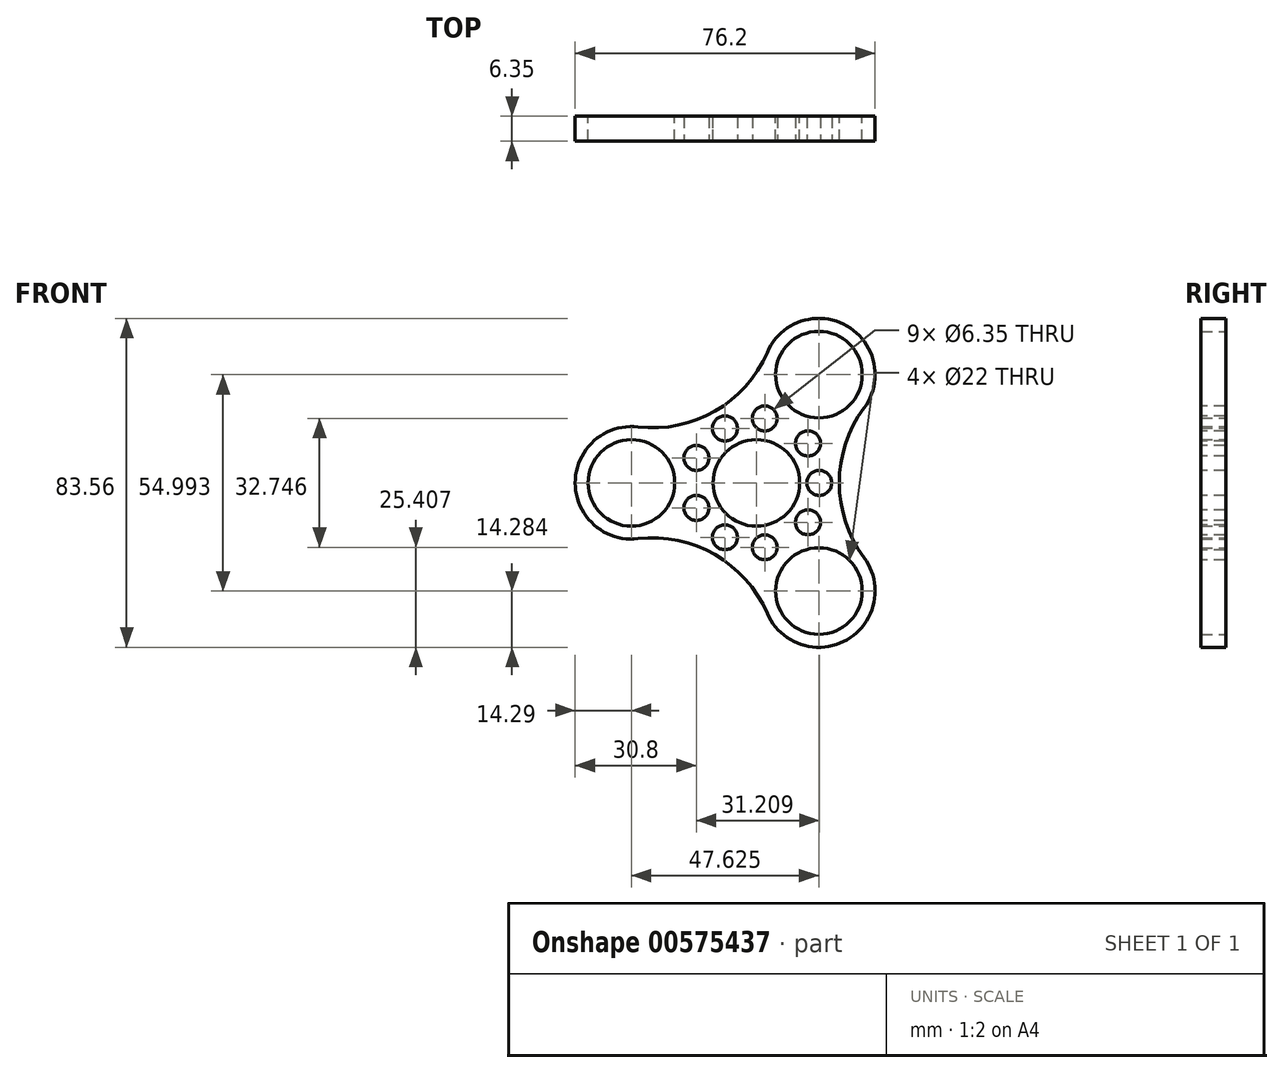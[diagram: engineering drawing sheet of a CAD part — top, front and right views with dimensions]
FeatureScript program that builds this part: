
annotation { "Feature Type Name" : "Feature", "Feature Type Description" : "" }
export const myFeature = defineFeature(function(context is Context, id is Id, definition is map)
    precondition{}
    {
        {
            var Q0;
            Q0=qCreatedBy(makeId("Front.planeOp"),FACE);
            var sketch = newSketch(context, id + "F0", { "sketchPlane" : qUnion([Q0])});
            skCircle(sketch, "E0", {"center": v(0, 0) * mm, "radius": 14.29 * mm});
            skCircle(sketch, "E1", {"center": v(0, 0) * mm, "radius": 11 * mm});
            skCircle(sketch, "E2", {"center": v(-31.75, 0) * mm, "radius": 14.29 * mm});
            skCircle(sketch, "E3", {"center": v(-31.75, 0) * mm, "radius": 11 * mm});
            skCircle(sketch, "E4.1.0", {"center": v(15.87, -27.5) * mm, "radius": 14.29 * mm});
            skCircle(sketch, "E4.2.0", {"center": v(15.88, 27.5) * mm, "radius": 14.29 * mm});
            skCircle(sketch, "E5", {"center": v(15.88, 27.5) * mm, "radius": 11 * mm});
            skCircle(sketch, "E6", {"center": v(15.87, -27.5) * mm, "radius": 11 * mm});
            skSolve(sketch);
        }
        {
            var Q0;
            Q0=makeQuery(id+"FFv1Rk9DyuZzD2w_0.imprint","IMPRINT",FACE,{"disambiguationData":[TD([[makeQuery(id+"FFv1Rk9DyuZzD2w_0.imprint","IMPRINT",EDGE,{"derivedFrom":sQuery(id+"FFv1Rk9DyuZzD2w_0.wireOp",EDGE,"BiCupdTj-Y5xa-yT44-ajqj-lFmwiwwpYxpl")}),1.0]])]});
            var sketch = newSketch(context, id + "F1", { "sketchPlane" : qUnion([Q0])});
            skCircle(sketch, "E7", {"center": v(0, 46.13) * mm, "radius": 31.85 * mm});
            skCircle(sketch, "E8", {"center": v(-29.85, 35.03) * mm, "radius": 20.68 * mm});
            skCircle(sketch, "E9", {"center": v(29.93, 35.25) * mm, "radius": 20.68 * mm});
            skCircle(sketch, "E10", {"center": v(0, -46.09) * mm, "radius": 31.8 * mm});
            skCircle(sketch, "E11", {"center": v(-29.8, -35.02) * mm, "radius": 20.68 * mm});
            skCircle(sketch, "E12", {"center": v(29.8, -35.02) * mm, "radius": 20.68 * mm});
            skSolve(sketch);
        }
        {
            var Q0;
            Q0=qCreatedBy(makeId("Front.planeOp"),FACE);
            var sketch = newSketch(context, id + "F2", { "sketchPlane" : qUnion([Q0])});
            skCircle(sketch, "E13.0", {"center": v(-31.75, 0) * mm, "radius": 14.29 * mm});
            skCircle(sketch, "E14.0", {"center": v(15.88, 27.5) * mm, "radius": 14.29 * mm});
            skCircle(sketch, "E15.0", {"center": v(15.87, -27.5) * mm, "radius": 14.29 * mm});
            skCircle(sketch, "E16.0", {"center": v(0, 0) * mm, "radius": 14.29 * mm});
            skCircle(sketch, "E17.0", {"center": v(-31.75, 0) * mm, "radius": 11 * mm});
            skCircle(sketch, "E18.0", {"center": v(0, 0) * mm, "radius": 11 * mm});
            skCircle(sketch, "E19.0", {"center": v(15.87, -27.5) * mm, "radius": 11 * mm});
            skCircle(sketch, "E20.0", {"center": v(15.88, 27.5) * mm, "radius": 11 * mm});
            skArc(sketch, "E21", {"start": v(27.33, 18.96) * mm, "mid": v(21.05, 0) * mm, "end": v(27.33, -18.96) * mm});
            skArc(sketch, "E22", {"start": v(2.76, -33.15) * mm, "mid": v(-10.52, -18.23) * mm, "end": v(-30.09, -14.2) * mm});
            skArc(sketch, "E23", {"start": v(-30.09, 14.2) * mm, "mid": v(-10.52, 18.23) * mm, "end": v(2.76, 33.15) * mm});
            skSolve(sketch);
        }
        {
            var Q0;
            Q0=makeQuery(id+"F2.imprint","IMPRINT",FACE,{"disambiguationData":[TD([[makeQuery(id+"F2.imprint","IMPRINT",EDGE,{"derivedFrom":sQuery(id+"F2.wireOp",EDGE,"E20.0")}),-1.0]])]});
            var Q1;
            {var subQ6=sQuery(id+"F2.wireOp",EDGE,"E16.0");Q1=makeQuery(id+"F2.imprint","IMPRINT",FACE,{"disambiguationData":[TD([[makeQuery(id+"F2.imprint","IMPRINT",EDGE,{"derivedFrom":subQ6}),-1.0]])]});}
            var Q2;
            Q2=makeQuery(id+"F2.imprint","IMPRINT",FACE,{"disambiguationData":[TD([[makeQuery(id+"F2.imprint","IMPRINT",EDGE,{"derivedFrom":sQuery(id+"F2.wireOp",EDGE,"E16.0")}),1.0]])]});
            var Q3;
            Q3=makeQuery(id+"F2.imprint","IMPRINT",FACE,{"disambiguationData":[TD([[makeQuery(id+"F2.imprint","IMPRINT",EDGE,{"derivedFrom":sQuery(id+"F2.wireOp",EDGE,"E17.0")}),-1.0]])]});
            var Q4;
            Q4=makeQuery(id+"F2.imprint","IMPRINT",FACE,{"disambiguationData":[TD([[makeQuery(id+"F2.imprint","IMPRINT",EDGE,{"derivedFrom":sQuery(id+"F2.wireOp",EDGE,"E19.0")}),-1.0]])]});
            extrude(context, id + "F3", {"entities" : qUnion([Q0, Q1, Q2, Q3, Q4]), "depth" : 6.35 * mm, "offsetDistance" : 25.4 * mm});
        }
        {
            var Q0;
            Q0=makeQuery(id+"F3.opExtrude","CAP_FACE",FACE,{"disambiguationData":[OSD([sQuery(id+"F2.wireOp",EDGE,"E13.0"),sQuery(id+"F2.wireOp",EDGE,"E14.0"),sQuery(id+"F2.wireOp",EDGE,"E15.0"),sQuery(id+"F2.wireOp",EDGE,"E17.0"),sQuery(id+"F2.wireOp",EDGE,"E18.0"),sQuery(id+"F2.wireOp",EDGE,"E19.0"),sQuery(id+"F2.wireOp",EDGE,"E20.0"),sQuery(id+"F2.wireOp",EDGE,"E21"),sQuery(id+"F2.wireOp",EDGE,"E22"),sQuery(id+"F2.wireOp",EDGE,"E23")])],"isStart":false});
            var sketch = newSketch(context, id + "F4", { "sketchPlane" : qUnion([Q0])});
            skCircle(sketch, "E24", {"center": v(-15.24, 6.35) * mm, "radius": 3.18 * mm});
            skCircle(sketch, "E25", {"center": v(-15.24, -6.35) * mm, "radius": 3.18 * mm});
            skCircle(sketch, "E26.1.0", {"center": v(2.12, -16.37) * mm, "radius": 3.18 * mm});
            skCircle(sketch, "E26.1.1", {"center": v(13.12, -10.02) * mm, "radius": 3.18 * mm});
            skCircle(sketch, "E26.2.0", {"center": v(13.12, 10.02) * mm, "radius": 3.18 * mm});
            skCircle(sketch, "E26.2.1", {"center": v(2.12, 16.37) * mm, "radius": 3.18 * mm});
            skPoint(sketch, "E26.center", {"position": v(0, 0) * mm});
            skSolve(sketch);
        }
        {
            var Q0;
            Q0=makeQuery(id+"F4.imprint","IMPRINT",FACE,{"disambiguationData":[TD([[makeQuery(id+"F4.imprint","IMPRINT",EDGE,{"derivedFrom":sQuery(id+"F4.wireOp",EDGE,"E24")}),-1.0]])]});
            var sketch = newSketch(context, id + "F5", { "sketchPlane" : qUnion([Q0])});
            skCircle(sketch, "E27", {"center": v(15.97, 0) * mm, "radius": 3.18 * mm});
            skCircle(sketch, "E28.1.0", {"center": v(-7.98, 13.83) * mm, "radius": 3.18 * mm});
            skCircle(sketch, "E28.2.0", {"center": v(-7.98, -13.83) * mm, "radius": 3.18 * mm});
            skPoint(sketch, "E28.center", {"position": v(0, 0) * mm});
            skSolve(sketch);
        }
        {
            var Q0;
            Q0=makeQuery(id+"F4.imprint","IMPRINT",FACE,{"disambiguationData":[TD([[makeQuery(id+"F4.imprint","IMPRINT",EDGE,{"derivedFrom":sQuery(id+"F4.wireOp",EDGE,"E24")}),1.0]])]});
            var Q1;
            Q1=makeQuery(id+"F5.imprint","IMPRINT",FACE,{"disambiguationData":[TD([[makeQuery(id+"F5.imprint","IMPRINT",EDGE,{"derivedFrom":sQuery(id+"F5.wireOp",EDGE,"E28.1.0")}),1.0]])]});
            var Q2;
            Q2=makeQuery(id+"F4.imprint","IMPRINT",FACE,{"disambiguationData":[TD([[makeQuery(id+"F4.imprint","IMPRINT",EDGE,{"derivedFrom":sQuery(id+"F4.wireOp",EDGE,"E26.2.1")}),1.0]])]});
            var Q3;
            Q3=makeQuery(id+"F4.imprint","IMPRINT",FACE,{"disambiguationData":[TD([[makeQuery(id+"F4.imprint","IMPRINT",EDGE,{"derivedFrom":sQuery(id+"F4.wireOp",EDGE,"E26.2.0")}),1.0]])]});
            var Q4;
            Q4=makeQuery(id+"F5.imprint","IMPRINT",FACE,{"disambiguationData":[TD([[makeQuery(id+"F5.imprint","IMPRINT",EDGE,{"derivedFrom":sQuery(id+"F5.wireOp",EDGE,"E27")}),1.0]])]});
            var Q5;
            Q5=makeQuery(id+"F4.imprint","IMPRINT",FACE,{"disambiguationData":[TD([[makeQuery(id+"F4.imprint","IMPRINT",EDGE,{"derivedFrom":sQuery(id+"F4.wireOp",EDGE,"E26.1.1")}),1.0]])]});
            var Q6;
            Q6=makeQuery(id+"F4.imprint","IMPRINT",FACE,{"disambiguationData":[TD([[makeQuery(id+"F4.imprint","IMPRINT",EDGE,{"derivedFrom":sQuery(id+"F4.wireOp",EDGE,"E26.1.0")}),1.0]])]});
            var Q7;
            Q7=makeQuery(id+"F5.imprint","IMPRINT",FACE,{"disambiguationData":[TD([[makeQuery(id+"F5.imprint","IMPRINT",EDGE,{"derivedFrom":sQuery(id+"F5.wireOp",EDGE,"E28.2.0")}),1.0]])]});
            var Q8;
            Q8=makeQuery(id+"F4.imprint","IMPRINT",FACE,{"disambiguationData":[TD([[makeQuery(id+"F4.imprint","IMPRINT",EDGE,{"derivedFrom":sQuery(id+"F4.wireOp",EDGE,"E25")}),1.0]])]});
            extrude(context, id + "F6", {"entities" : qUnion([Q0, Q1, Q2, Q3, Q4, Q5, Q6, Q7, Q8]), "operationType" : NewBodyOperationType.REMOVE, "endBound" : BoundingType.THROUGH_ALL, "oppositeDirection" : true, "depth" : 25.4 * mm, "offsetDistance" : 25.4 * mm});
        }
    });
